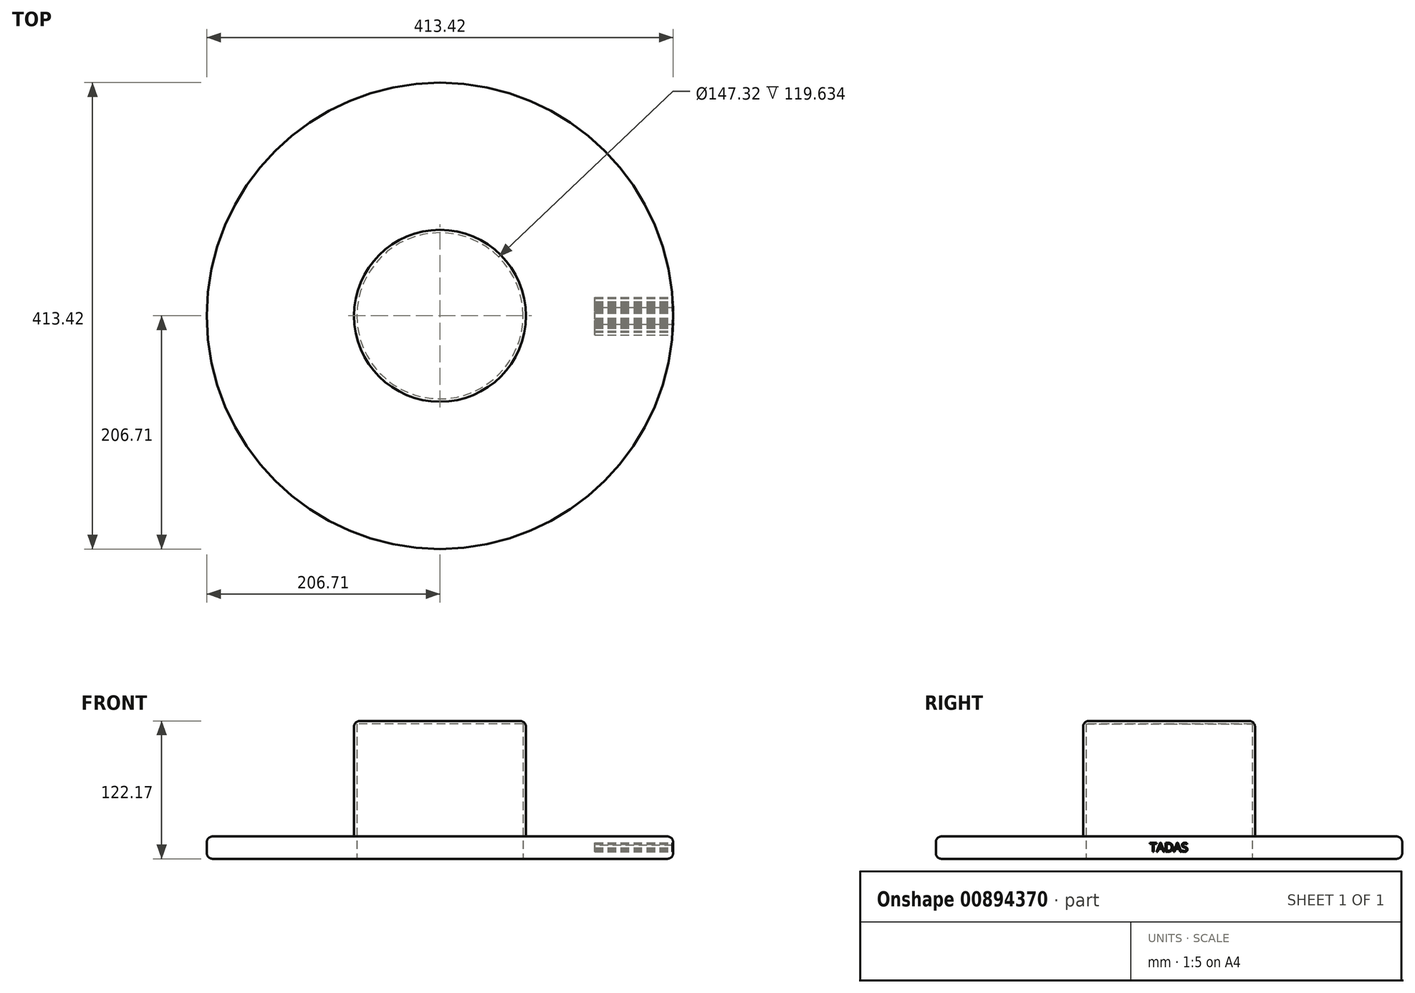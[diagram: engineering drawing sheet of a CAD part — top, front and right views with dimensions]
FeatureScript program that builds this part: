
annotation { "Feature Type Name" : "Feature", "Feature Type Description" : "" }
export const myFeature = defineFeature(function(context is Context, id is Id, definition is map)
    precondition{}
    {
        {
            var Q0;
            Q0=qCreatedBy(makeId("Top.planeOp"),FACE);
            var sketch = newSketch(context, id + "F0", { "sketchPlane" : qUnion([Q0])});
            skCircle(sketch, "E0", {"center": v(0, 0) * mm, "radius": 76.2 * mm});
            skCircle(sketch, "E1", {"center": v(0, 0) * mm, "radius": 206.71 * mm});
            skSolve(sketch);
        }
        {
            var Q0;
            Q0=makeQuery(id+"F0.imprint","IMPRINT",FACE,{"disambiguationData":[TD([[makeQuery(id+"F0.imprint","IMPRINT",EDGE,{"derivedFrom":sQuery(id+"F0.wireOp",EDGE,"E0")}),1.0]])]});
            extrude(context, id + "F1", {"entities" : qUnion([Q0]), "depth" : 122.17 * mm, "offsetDistance" : 25.4 * mm});
        }
        {
            var Q0;
            Q0=makeQuery(id+"F1.opExtrude","CAP_FACE",FACE,{"disambiguationData":[OSD([sQuery(id+"F0.wireOp",EDGE,"E0")])],"isStart":true});
            shell(context, id + "F2", {"entities" : qUnion([Q0]), "thickness" : 2.54 * mm});
        }
        {
            var Q0;
            Q0 = qSketchRegion(id + "F0", true);
            extrude(context, id + "F3", {"entities" : qUnion([Q0]), "operationType" : NewBodyOperationType.ADD, "depth" : 19.8 * mm, "offsetDistance" : 25.4 * mm});
        }
        {
            var Q0;
            Q0=makeQuery(id+"F3.opExtrude","CAP_EDGE",EDGE,{"disambiguationData":[OSD([sQuery(id+"F0.wireOp",EDGE,"A1ea822o-b5iI-u1Bp-9tVa-Z8u6LcKYP1vI")])],"isStart":false});
            var Q1;
            Q1=makeQuery(id+"F1.opExtrude","CAP_EDGE",EDGE,{"disambiguationData":[OSD([sQuery(id+"F0.wireOp",EDGE,"E0")])],"isStart":false});
            var Q2;
            Q2=makeQuery(id+"F3.opExtrude","CAP_EDGE",EDGE,{"disambiguationData":[OSD([sQuery(id+"F0.wireOp",EDGE,"A1ea822o-b5iI-u1Bp-9tVa-Z8u6LcKYP1vI")])],"isStart":true});
            var Q3;
            Q3=makeQuery(id+"F3.opExtrude","CAP_EDGE",EDGE,{"disambiguationData":[OSD([sQuery(id+"F0.wireOp",EDGE,"E1")])],"isStart":false});
            var Q4;
            Q4=makeQuery(id+"F3.opExtrude","CAP_EDGE",EDGE,{"disambiguationData":[OSD([sQuery(id+"F0.wireOp",EDGE,"E1")])],"isStart":true});
            fillet(context, id + "F4", {"entities" : qUnion([Q0, Q1, Q2, Q3, Q4]), "radius" : 5.08 * mm, "tangentPropagation" : true, "allowEdgeOverflow" : false});
        }
        {
            var Q0;
            Q0=qCreatedBy(makeId("Right.planeOp"),FACE);
            cPlane(context, id + "F5", {"entities" : qUnion([Q0]), "cplaneType" : CPlaneType.OFFSET, "offset" : 208.79 * mm, "width" : 152.4 * mm, "height" : 152.4 * mm});
        }
        {
            var Q0;
            Q0=qCreatedBy(id+"F5.planeOp",FACE);
            var sketch = newSketch(context, id + "F6", { "sketchPlane" : qUnion([Q0])});
            skText(sketch, "E2", { "text": "TADAS", "fontName": "OpenSans-Regular.ttf"});
            const initialGuessF6  = {"E2": [-0.01705, 0.00627, 1, 0, 0.00788]};
            skSetInitialGuess(sketch, initialGuessF6);
            skSolve(sketch);
        }
        {
            var Q0;
            Q0 = qSketchRegion(id + "F6", true);
            extrude(context, id + "F7", {"entities" : qUnion([Q0]), "operationType" : NewBodyOperationType.REMOVE, "oppositeDirection" : true, "depth" : 71.63 * mm, "offsetDistance" : 25.4 * mm});
        }
    });
